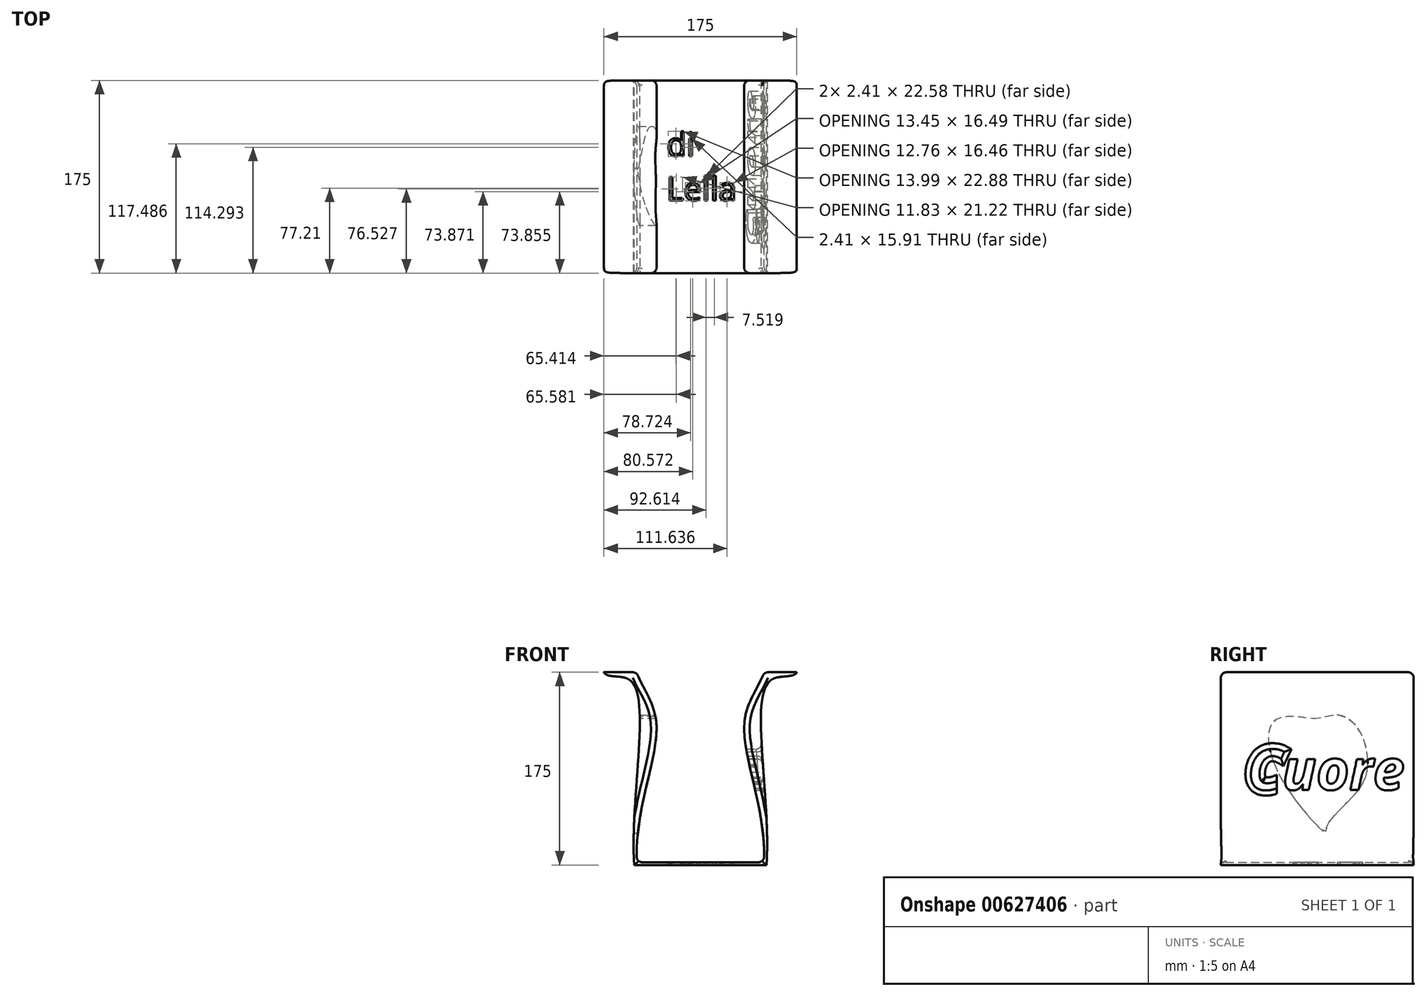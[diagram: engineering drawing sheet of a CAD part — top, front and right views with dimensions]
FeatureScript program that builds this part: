
annotation { "Feature Type Name" : "Feature", "Feature Type Description" : "" }
export const myFeature = defineFeature(function(context is Context, id is Id, definition is map)
    precondition{}
    {
        {
            var Q0;
            Q0=qCreatedBy(makeId("Front.planeOp"),FACE);
            var sketch = newSketch(context, id + "F0", { "sketchPlane" : qUnion([Q0])});
            skLineSegment(sketch, "E0", {"start": v(-60, -68.17) * mm, "end": v(0, -68.17) * mm});
            skLineSegment(sketch, "E1", {"start": v(0, 136.89) * mm, "end": v(0, -156.21) * mm, "construction": true});
            skLineSegment(sketch, "E2.MirrorCS", {"start": v(60, -68.17) * mm, "end": v(0, -68.17) * mm});
            skPoint(sketch, "E3.end.orphan", {"position": v(87.5, 106.83) * mm});
            skPoint(sketch, "E3.start.orphan", {"position": v(0, 106.83) * mm});
            skPoint(sketch, "E4.MirrorCS.end.orphan", {"position": v(-87.5, 106.83) * mm});
            skLineSegment(sketch, "E5", {"start": v(-87.5, 106.83) * mm, "end": v(87.5, 106.83) * mm, "construction": true});
            skLineSegment(sketch, "E6", {"start": v(87.5, 106.83) * mm, "end": v(60, -68.17) * mm, "construction": true});
            skLineSegment(sketch, "E7", {"start": v(60, -68.17) * mm, "end": v(60, 133.84) * mm, "construction": true});
            skFitSpline(sketch, "E8", {"points": [v(87.5, 106.83) * mm, v(63.12, 99.04) * mm, v(60, -68.17) * mm], "startDerivative": vector(-41.26, -65.74) * mm, "endDerivative": vector(-16.93, -258.92) * mm});
            skFitSpline(sketch, "E9.MirrorCS", {"points": [v(-87.5, 106.83) * mm, v(-63.12, 99.04) * mm, v(-60, -68.17) * mm], "startDerivative": vector(41.26, -65.74) * mm, "endDerivative": vector(16.93, -258.92) * mm});
            skLineSegment(sketch, "E10", {"start": v(87.5, 106.83) * mm, "end": v(57.5, 106.83) * mm});
            skLineSegment(sketch, "E11.0", {"start": v(53.93, -65.67) * mm, "end": v(0, -65.67) * mm});
            skLineSegment(sketch, "E12.0", {"start": v(-60, -65.67) * mm, "end": v(0, -65.67) * mm});
            skPoint(sketch, "E13.start.orphan", {"position": v(53.93, -65.67) * mm});
            skLineSegment(sketch, "E14", {"start": v(53.93, -65.67) * mm, "end": v(60.15, -65.67) * mm});
            skLineSegment(sketch, "E15", {"start": v(57.65, -65.67) * mm, "end": v(60.15, -65.67) * mm});
            skFitSpline(sketch, "E16", {"points": [v(57.5, 106.83) * mm, v(40.24, 63.89) * mm, v(57.65, -65.67) * mm], "startDerivative": vector(-19.17, -88.7) * mm, "endDerivative": vector(-11.33, -240.28) * mm});
            skFitSpline(sketch, "E17.MirrorCS", {"points": [v(-57.5, 106.83) * mm, v(-40.24, 63.89) * mm, v(-57.65, -65.67) * mm], "startDerivative": vector(19.17, -88.7) * mm, "endDerivative": vector(11.33, -240.28) * mm});
            skLineSegment(sketch, "E18.MirrorCS", {"start": v(-87.5, 106.83) * mm, "end": v(-57.5, 106.83) * mm});
            skLineSegment(sketch, "E19", {"start": v(-87.5, 106.83) * mm, "end": v(-87.5, 94.94) * mm});
            skLineSegment(sketch, "E20", {"start": v(-87.5, 94.94) * mm, "end": v(-63.12, 99.04) * mm});
            skLineSegment(sketch, "E21.MirrorCS", {"start": v(87.5, 106.83) * mm, "end": v(87.5, 94.94) * mm});
            skLineSegment(sketch, "E22", {"start": v(87.5, 94.94) * mm, "end": v(63.12, 99.04) * mm});
            skSolve(sketch);
        }
        {
            var Q0;
            {var subQ0=sQuery(id+"F0.wireOp",EDGE,"E10");Q0=makeQuery(id+"F0.imprint","IMPRINT",FACE,{"disambiguationData":[TD([[makeQuery(id+"F0.imprint","IMPRINT",EDGE,{"derivedFrom":subQ0}),1.0]])]});}
            var Q1;
            Q1=makeQuery(id+"F0.imprint","IMPRINT",FACE,{"disambiguationData":[TD([[makeQuery(id+"F0.imprint","IMPRINT",EDGE,{"derivedFrom":sQuery(id+"F0.wireOp",EDGE,"E0")}),1.0]])]});
            extrude(context, id + "F1", {"entities" : qUnion([Q0, Q1]), "depth" : 175 * mm, "offsetDistance" : 25 * mm});
        }
        {
            var Q0;
            Q0=makeQuery(id+"F1.opExtrude","SWEPT_EDGE",EDGE,{"disambiguationData":[OSD([sQuery(id+"F0.wireOp",EDGE,"E17.MirrorCS"),sQuery(id+"F0.wireOp",EDGE,"E18.MirrorCS")])]});
            var Q1;
            Q1=makeQuery(id+"F1.opExtrude","SWEPT_EDGE",EDGE,{"disambiguationData":[OSD([sQuery(id+"F0.wireOp",EDGE,"E10"),sQuery(id+"F0.wireOp",EDGE,"E16")])]});
            var Q2;
            Q2=makeQuery(id+"F1.opExtrude","SWEPT_EDGE",EDGE,{"disambiguationData":[OSD([sQuery(id+"F0.wireOp",EDGE,"E12.0"),sQuery(id+"F0.wireOp",EDGE,"E17.MirrorCS")])]});
            var Q3;
            Q3=makeQuery(id+"F1.opExtrude","SWEPT_EDGE",EDGE,{"disambiguationData":[OSD([sQuery(id+"F0.wireOp",EDGE,"E14"),sQuery(id+"F0.wireOp",EDGE,"E15"),sQuery(id+"F0.wireOp",EDGE,"E16")])]});
            fillet(context, id + "F2", {"entities" : qUnion([Q0, Q1, Q2, Q3]), "radius" : 5 * mm, "tangentPropagation" : true, "allowEdgeOverflow" : false});
        }
        {
            var Q0;
            Q0=qCreatedBy(makeId("Right.planeOp"),FACE);
            cPlane(context, id + "F3", {"entities" : qUnion([Q0]), "cplaneType" : CPlaneType.OFFSET, "offset" : 80 * mm, "width" : 150 * mm, "height" : 150 * mm});
        }
        {
            var Q0;
            Q0=qCreatedBy(id+"F3.planeOp",FACE);
            var sketch = newSketch(context, id + "F4", { "sketchPlane" : qUnion([Q0])});
            skText(sketch, "E23", { "text": "Cuore\n", "fontName": "OpenSans-BoldItalic.ttf"});
            const initialGuessF4  = {"E23": [-0.15076, 0, 1, 0, 0.0369]};
            skSetInitialGuess(sketch, initialGuessF4);
            skSolve(sketch);
        }
        {
            var Q0;
            Q0=makeQuery(id+"F4.imprint","IMPRINT",FACE,{"disambiguationData":[TD([[makeQuery(id+"F4.imprint","IMPRINT",EDGE,{"derivedFrom":sQuery(id+"F4.wireOp",EDGE,"E23.sketch_text.stroke-53")}),-1.0]])]});
            var Q1;
            Q1=makeQuery(id+"F4.imprint","IMPRINT",FACE,{"disambiguationData":[TD([[makeQuery(id+"F4.imprint","IMPRINT",EDGE,{"derivedFrom":sQuery(id+"F4.wireOp",EDGE,"E23.sketch_text.stroke-0")}),-1.0]])]});
            var Q2;
            Q2=makeQuery(id+"F4.imprint","IMPRINT",FACE,{"disambiguationData":[TD([[makeQuery(id+"F4.imprint","IMPRINT",EDGE,{"derivedFrom":sQuery(id+"F4.wireOp",EDGE,"E23.sketch_text.stroke-18")}),-1.0]])]});
            var Q3;
            Q3=makeQuery(id+"F4.imprint","IMPRINT",FACE,{"disambiguationData":[TD([[makeQuery(id+"F4.imprint","IMPRINT",EDGE,{"derivedFrom":sQuery(id+"F4.wireOp",EDGE,"E23.sketch_text.stroke-35")}),-1.0]])]});
            var Q4;
            Q4=makeQuery(id+"F4.imprint","IMPRINT",FACE,{"disambiguationData":[TD([[makeQuery(id+"F4.imprint","IMPRINT",EDGE,{"derivedFrom":sQuery(id+"F4.wireOp",EDGE,"E23.sketch_text.stroke-65")}),-1.0]])]});
            extrude(context, id + "F5", {"entities" : qUnion([Q0, Q1, Q2, Q3, Q4]), "operationType" : NewBodyOperationType.REMOVE, "oppositeDirection" : true, "depth" : 50 * mm, "offsetDistance" : 25 * mm});
        }
        {
            var Q0;
            Q0=qCreatedBy(makeId("Right.planeOp"),FACE);
            cPlane(context, id + "F6", {"entities" : qUnion([Q0]), "cplaneType" : CPlaneType.OFFSET, "offset" : 150 * mm, "oppositeDirection" : true, "width" : 150 * mm, "height" : 150 * mm});
        }
        {
            var Q0;
            Q0=qCreatedBy(id+"F6.planeOp",FACE);
            var sketch = newSketch(context, id + "F7", { "sketchPlane" : qUnion([Q0])});
            skFitSpline(sketch, "E24", {"points": [v(-85.99, 65.1) * mm, v(-66.98, 67.76) * mm, v(-48.18, 52.03) * mm, v(-41.64, 24.24) * mm, v(-50.02, 0) * mm, v(-79.85, -35.03) * mm, v(-79.65, -39.52) * mm, v(-119.7, 9.52) * mm, v(-127.47, 61.63) * mm, v(-102.74, 66.13) * mm, v(-85.99, 65.1) * mm]});
            skSolve(sketch);
        }
        {
            var Q0;
            Q0=makeQuery(id+"F7.imprint","IMPRINT",FACE,{"disambiguationData":[TD([[makeQuery(id+"F7.imprint","IMPRINT",EDGE,{"derivedFrom":sQuery(id+"F7.wireOp",EDGE,"E24")}),-1.0]])]});
            extrude(context, id + "F8", {"entities" : qUnion([Q0]), "operationType" : NewBodyOperationType.REMOVE, "depth" : 100 * mm, "offsetDistance" : 25 * mm});
        }
        {
            var Q0;
            Q0=makeQuery(id+"F1.opExtrude","SWEPT_FACE",FACE,{"disambiguationData":[OSD([sQuery(id+"F0.wireOp",EDGE,"E11.0"),sQuery(id+"F0.wireOp",EDGE,"E12.0"),sQuery(id+"F0.wireOp",EDGE,"E14")])]});
            var sketch = newSketch(context, id + "F9", { "sketchPlane" : qUnion([Q0])});
            skText(sketch, "E25", { "text": "di\nLella", "fontName": "OpenSans-Regular.ttf"});
            const initialGuessF9  = {"E25": [-0.03075, -0.06866, 1, 0, 0.0214]};
            skSetInitialGuess(sketch, initialGuessF9);
            skSolve(sketch);
        }
        {
            var Q0;
            Q0=makeQuery(id+"F9.imprint","IMPRINT",FACE,{"disambiguationData":[TD([[makeQuery(id+"F9.imprint","IMPRINT",EDGE,{"derivedFrom":sQuery(id+"F9.wireOp",EDGE,"E25.sketch_text.stroke-65")}),-1.0]])]});
            var Q1;
            Q1=qSketchRegion(id+"F9",true);
            var Q2;
            Q2=makeQuery(id+"F9.imprint","IMPRINT",FACE,{"disambiguationData":[TD([[makeQuery(id+"F9.imprint","IMPRINT",EDGE,{"derivedFrom":sQuery(id+"F9.wireOp",EDGE,"E25.sketch_text.stroke-36")}),-1.0]])]});
            var Q3;
            Q3=makeQuery(id+"F9.imprint","IMPRINT",FACE,{"disambiguationData":[TD([[makeQuery(id+"F9.imprint","IMPRINT",EDGE,{"derivedFrom":sQuery(id+"F9.wireOp",EDGE,"E25.sketch_text.stroke-69")}),-1.0]])]});
            var Q4;
            Q4=makeQuery(id+"F9.imprint","IMPRINT",FACE,{"disambiguationData":[TD([[makeQuery(id+"F9.imprint","IMPRINT",EDGE,{"derivedFrom":sQuery(id+"F9.wireOp",EDGE,"E25.sketch_text.stroke-61")}),-1.0]])]});
            var Q5;
            Q5=makeQuery(id+"F9.imprint","IMPRINT",FACE,{"disambiguationData":[TD([[makeQuery(id+"F9.imprint","IMPRINT",EDGE,{"derivedFrom":sQuery(id+"F9.wireOp",EDGE,"E25.sketch_text.stroke-42")}),-1.0]])]});
            var Q6;
            Q6=makeQuery(id+"F9.imprint","IMPRINT",FACE,{"disambiguationData":[TD([[makeQuery(id+"F9.imprint","IMPRINT",EDGE,{"derivedFrom":sQuery(id+"F9.wireOp",EDGE,"E25.sketch_text.stroke-28")}),-1.0]])]});
            var Q7;
            Q7=makeQuery(id+"F9.imprint","IMPRINT",FACE,{"disambiguationData":[TD([[makeQuery(id+"F9.imprint","IMPRINT",EDGE,{"derivedFrom":sQuery(id+"F9.wireOp",EDGE,"E25.sketch_text.stroke-0")}),-1.0]])]});
            var Q8;
            Q8=makeQuery(id+"F9.imprint","IMPRINT",FACE,{"disambiguationData":[TD([[makeQuery(id+"F9.imprint","IMPRINT",EDGE,{"derivedFrom":sQuery(id+"F9.wireOp",EDGE,"E25.sketch_text.stroke-24")}),-1.0]])]});
            extrude(context, id + "F10", {"entities" : qUnion([Q0, Q1, Q2, Q3, Q4, Q5, Q6, Q7, Q8]), "operationType" : NewBodyOperationType.REMOVE, "oppositeDirection" : true, "depth" : 70 * mm, "offsetDistance" : 25 * mm});
        }
        {
            var Q0;
            Q0=makeQuery(id+"F1.opExtrude","CAP_EDGE",EDGE,{"disambiguationData":[OSD([sQuery(id+"F0.wireOp",EDGE,"E11.0"),sQuery(id+"F0.wireOp",EDGE,"E12.0"),sQuery(id+"F0.wireOp",EDGE,"E14")])],"isStart":false});
            var Q1;
            Q1=makeQuery(id+"F1.opExtrude","CAP_EDGE",EDGE,{"disambiguationData":[OSD([sQuery(id+"F0.wireOp",EDGE,"E16")])],"isStart":true});
            fillet(context, id + "F11", {"entities" : qUnion([Q0, Q1]), "radius" : 5 * mm, "tangentPropagation" : true, "allowEdgeOverflow" : false});
        }
        {
            var Q0;
            Q0=makeQuery(id+"F8.boolean.opBoolean","COPY",FACE,{"derivedFrom":makeQuery(id+"F8.opExtrude","CAP_FACE",FACE,{"disambiguationData":[OSD([sQuery(id+"F7.wireOp",EDGE,"E24")])],"isStart":false})});
            extrude(context, id + "F12", {"entities" : qUnion([Q0]), "operationType" : NewBodyOperationType.REMOVE, "oppositeDirection" : true, "depth" : 40 * mm, "offsetDistance" : 25 * mm});
        }
        {
            var Q0;
            Q0=makeQuery(id+"F5.boolean.opBoolean","INTERSECT",EDGE,{"derivedFrom":[makeQuery(id+"F1.opExtrude","SWEPT_FACE",FACE,{"disambiguationData":[OSD([sQuery(id+"F0.wireOp",EDGE,"E8")])]}),makeQuery(id+"F5.opExtrude","SWEPT_FACE",FACE,{"disambiguationData":[OSD([sQuery(id+"F4.wireOp",EDGE,"E23.sketch_text.stroke-3")])]})]});
            var Q1;
            Q1=makeQuery(id+"F5.boolean.opBoolean","INTERSECT",EDGE,{"derivedFrom":[makeQuery(id+"F1.opExtrude","SWEPT_FACE",FACE,{"disambiguationData":[OSD([sQuery(id+"F0.wireOp",EDGE,"E8")])]}),makeQuery(id+"F5.opExtrude","SWEPT_FACE",FACE,{"disambiguationData":[OSD([sQuery(id+"F4.wireOp",EDGE,"E23.sketch_text.stroke-8")])]})]});
            var Q2;
            Q2=makeQuery(id+"F5.boolean.opBoolean","INTERSECT",EDGE,{"derivedFrom":[makeQuery(id+"F1.opExtrude","SWEPT_FACE",FACE,{"disambiguationData":[OSD([sQuery(id+"F0.wireOp",EDGE,"E8")])]}),makeQuery(id+"F5.opExtrude","SWEPT_FACE",FACE,{"disambiguationData":[OSD([sQuery(id+"F4.wireOp",EDGE,"E23.sketch_text.stroke-15")])]})]});
            var Q3;
            {var subQ0=sQuery(id+"F0.wireOp",EDGE,"E10");var subQ10=sQuery(id+"F0.wireOp",EDGE,"E8");Q3=makeQuery(id+"F5.boolean.opBoolean","SPLIT",FACE,{"disambiguationData":[TD([makeQuery(id+"F1.opExtrude","SWEPT_FACE",FACE,{"disambiguationData":[OSD([subQ0])]})])],"derivedFrom":makeQuery(id+"F1.opExtrude","SWEPT_FACE",FACE,{"disambiguationData":[OSD([subQ10])]})});}
            fillet(context, id + "F13", {"entities" : qUnion([Q0, Q1, Q2, Q3]), "radius" : 5 * mm, "tangentPropagation" : true, "allowEdgeOverflow" : false});
        }
    });
